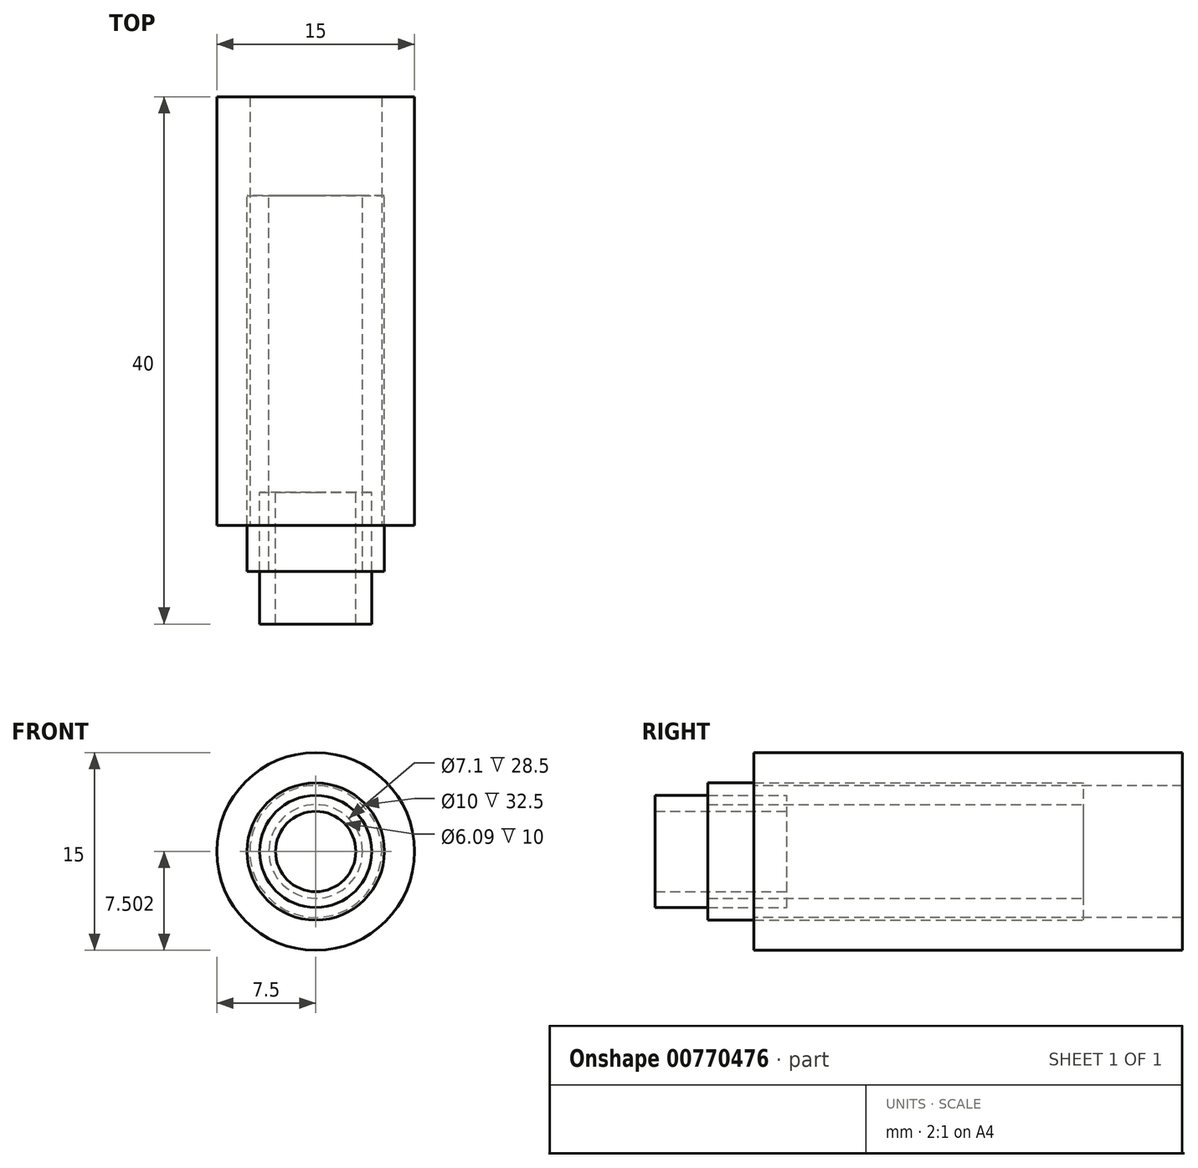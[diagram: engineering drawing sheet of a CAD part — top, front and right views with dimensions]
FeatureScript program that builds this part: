
annotation { "Feature Type Name" : "Feature", "Feature Type Description" : "" }
export const myFeature = defineFeature(function(context is Context, id is Id, definition is map)
    precondition{}
    {
        {
            var Q0;
            Q0=qCreatedBy(makeId("Front.planeOp"),FACE);
            var sketch = newSketch(context, id + "F0", { "sketchPlane" : qUnion([Q0])});
            skCircle(sketch, "E0", {"center": v(0, 15.76) * mm, "radius": 3.04 * mm});
            skCircle(sketch, "E1", {"center": v(0, 15.76) * mm, "radius": 4.25 * mm});
            skLineSegment(sketch, "E2", {"start": v(0, 15.76) * mm, "end": v(0, 0) * mm});
            skSolve(sketch);
        }
        {
            var Q0;
            Q0 = qSketchRegion(id + "F0", true);
            extrude(context, id + "F1", {"entities" : qUnion([Q0]), "depth" : 10 * mm, "offsetDistance" : 25 * mm});
        }
        {
            var Q0;
            Q0=qCreatedBy(makeId("Front.planeOp"),FACE);
            var sketch = newSketch(context, id + "F2", { "sketchPlane" : qUnion([Q0])});
            skLineSegment(sketch, "E3", {"start": v(0, 0) * mm, "end": v(0, 15.76) * mm});
            skCircle(sketch, "E4", {"center": v(0, 15.76) * mm, "radius": 5 * mm});
            skCircle(sketch, "E5", {"center": v(0, 15.76) * mm, "radius": 7.5 * mm});
            skSolve(sketch);
        }
        {
            var Q0;
            Q0 = qSketchRegion(id + "F2", true);
            extrude(context, id + "F3", {"entities" : qUnion([Q0]), "oppositeDirection" : true, "depth" : 30 * mm, "offsetDistance" : 25 * mm, "hasSecondDirection" : true, "secondDirectionOppositeDirection" : false, "secondDirectionDepth" : 2.5 * mm});
        }
        {
            var Q0;
            Q0=makeQuery(id+"F3.opExtrude","CAP_FACE",FACE,{"disambiguationData":[OSD([sQuery(id+"F2.wireOp",EDGE,"E4"),sQuery(id+"F2.wireOp",EDGE,"E5")])],"isStart":true});
            var sketch = newSketch(context, id + "F4", { "sketchPlane" : qUnion([Q0])});
            skCircle(sketch, "E6", {"center": v(0, 15.76) * mm, "radius": 5.2 * mm});
            skCircle(sketch, "E7", {"center": v(0, 15.76) * mm, "radius": 3.55 * mm});
            skSolve(sketch);
        }
        {
            var Q0;
            Q0 = qSketchRegion(id + "F4", true);
            extrude(context, id + "F5", {"entities" : qUnion([Q0]), "depth" : 3.5 * mm, "offsetDistance" : 25 * mm, "hasSecondDirection" : true, "secondDirectionOppositeDirection" : true, "secondDirectionDepth" : 25 * mm});
        }
    });
